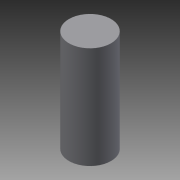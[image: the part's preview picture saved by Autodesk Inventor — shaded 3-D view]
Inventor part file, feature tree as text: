
AUTODESK INVENTOR PART (.ipt)
format: ipt  version: 2016 (Build 200138000, 138)  size: 82,432 bytes
history: native  units: mm
features: extrude x1, sketch x1
ambient origin geometry x8: Origin, YZ Plane, XZ Plane, XY Plane, X Axis, Y Axis, Z Axis, Center Point
bodies: Solid1 (feature_tree)
feature tree (2):
  extrude  "Extrusion1"  TaperAngle=0.0deg  [1 undecoded]
  sketch  "Sketch1"  dims[d2=0.0mm d3=0.0mm d4=0.0mm d9=0.0mm d10=0.0mm]
note: 1 required parameter value undecoded (feature->parameter linkage not recoverable at this tier; creation-order binding heuristic only, values carry confidence <= 0.55)
